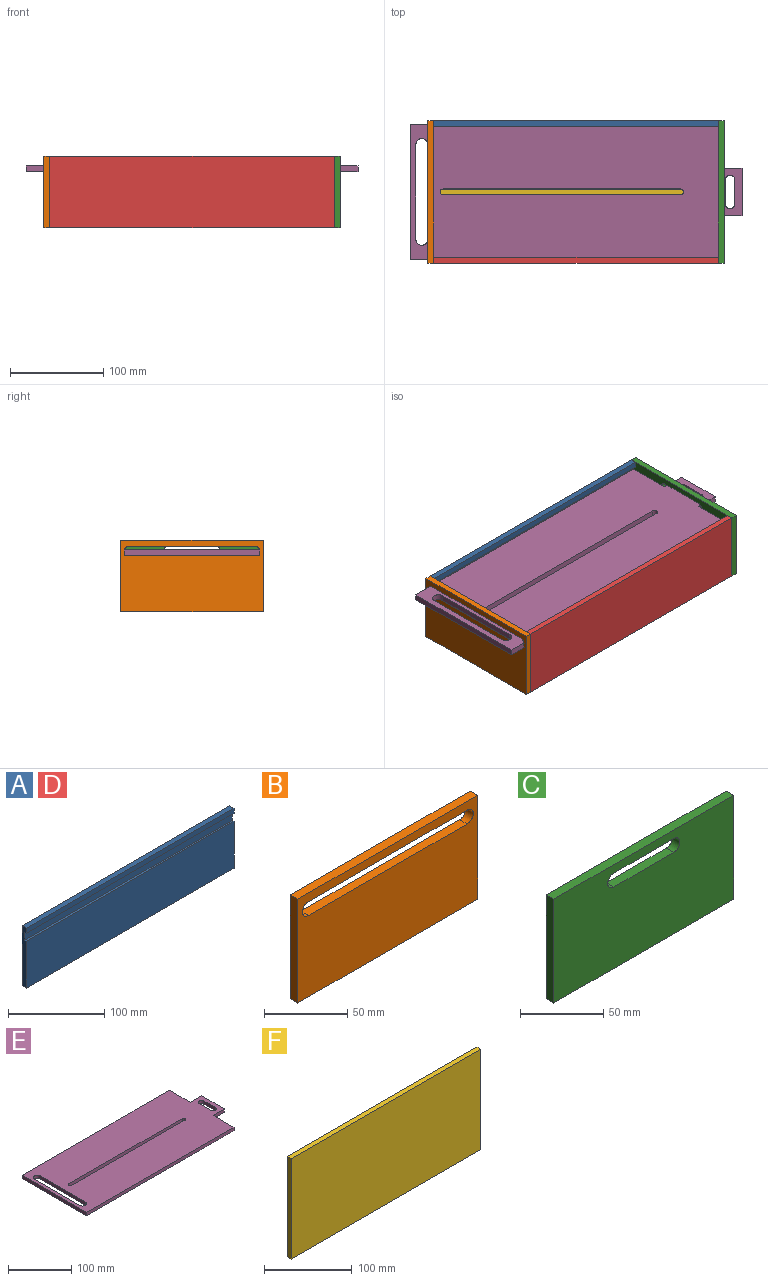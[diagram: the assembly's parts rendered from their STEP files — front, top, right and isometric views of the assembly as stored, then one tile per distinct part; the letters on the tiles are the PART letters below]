
ASSEMBLY  parts=6 mates=14
PART A: 10 faces, bbox 304.8x6.4x76.2 mm
  f0: plane 304.8x6.35mm, normal (0,-1,0), area 1935.5mm2, adj f1,f2,f4,f7
  f1: plane 76.2x6.35mm, normal (1,0,0), area 458.1mm2, adj f0,f3,f4,f5,f6,f7,f8,f9
  f2: plane 76.2x6.35mm, normal (-1,0,0), area 458.1mm2, adj f0,f3,f4,f5,f6,f7,f8,f9
  f3: plane 304.8x6.35mm, normal (0,0,-1), area 1935.5mm2, adj f1,f2,f5,f6
  f4: plane 304.8x6.35mm, normal (0,0,1), area 1935.5mm2, adj f0,f1,f2,f5
  f5: plane 304.8x76.2mm, normal (0,1,0), area 23225.8mm2, adj f1,f2,f3,f4
  f6: plane 304.8x59.69mm, normal (0,-1,0), area 18193.5mm2, adj f1,f2,f3,f8
  f7: plane 304.8x2.54mm, normal (0,0,-1), area 774.2mm2, adj f0,f1,f2,f9
  f8: plane 304.8x2.54mm, normal (0,0,1), area 774.2mm2, adj f1,f2,f6,f9
  f9: plane 304.8x10.16mm, normal (0,-1,0), area 3096.8mm2, adj f1,f2,f7,f8
PART B: 10 faces, bbox 152.4x6.4x76.2 mm
  f0: plane 152.4x6.35mm, normal (0,0,-1), area 967.7mm2, adj f1,f7,f8,f9
  f1: plane 76.2x6.35mm, normal (1,0,0), area 483.9mm2, adj f0,f2,f8,f9
  f2: plane 152.4x6.35mm, normal (0,0,1), area 967.7mm2, adj f1,f7,f8,f9
  f3: cylinder r=5.08mm len=10.16mm, axis (0,-1,0), area 101.3mm2, adj f4,f6,f8,f9
  f4: plane 134.62x6.35mm, normal (0,0,-1), area 854.8mm2, adj f3,f5,f8,f9
  f5: cylinder r=5.08mm len=10.16mm, axis (0,-1,0), area 101.3mm2, adj f4,f6,f8,f9
  f6: plane 134.62x6.35mm, normal (0,0,1), area 854.8mm2, adj f3,f5,f8,f9
  f7: plane 76.2x6.35mm, normal (-1,0,0), area 483.9mm2, adj f0,f2,f8,f9
  f8: plane 152.4x76.2mm, normal (0,1,0), area 10164.1mm2, adj f0,f1,f2,f3,f4,f5,f6,f7
  f9: plane 152.4x76.2mm, normal (0,-1,0), area 10164.1mm2, adj f0,f1,f2,f3,f4,f5,f6,f7
PART C: 10 faces, bbox 152.4x6.4x76.2 mm
  f0: plane 152.4x6.35mm, normal (0,0,-1), area 967.7mm2, adj f1,f7,f8,f9
  f1: plane 76.2x6.35mm, normal (1,0,0), area 483.9mm2, adj f0,f2,f8,f9
  f2: plane 152.4x6.35mm, normal (0,0,1), area 967.7mm2, adj f1,f7,f8,f9
  f3: cylinder r=5.08mm len=10.16mm, axis (0,-1,0), area 101.3mm2, adj f4,f6,f8,f9
  f4: plane 50.8x6.35mm, normal (0,0,-1), area 322.6mm2, adj f3,f5,f8,f9
  f5: cylinder r=5.08mm len=10.16mm, axis (0,-1,0), area 101.3mm2, adj f4,f6,f8,f9
  f6: plane 50.8x6.35mm, normal (0,0,1), area 322.6mm2, adj f3,f5,f8,f9
  f7: plane 76.2x6.35mm, normal (-1,0,0), area 483.9mm2, adj f0,f2,f8,f9
  f8: plane 152.4x76.2mm, normal (0,1,0), area 11015.7mm2, adj f0,f1,f2,f3,f4,f5,f6,f7
  f9: plane 152.4x76.2mm, normal (0,-1,0), area 11015.7mm2, adj f0,f1,f2,f3,f4,f5,f6,f7
PART D: same geometry as A
PART E: 22 faces, bbox 355.6x144.8x6.4 mm
  f0: plane 25.4x6.35mm, normal (0,1,0), area 161.3mm2, adj f1,f19,f20,f21
  f1: plane 46.99x6.35mm, normal (1,0,0), area 298.4mm2, adj f0,f2,f20,f21
  f2: plane 330.2x6.35mm, normal (0,1,0), area 2096.8mm2, adj f1,f3,f20,f21
  f3: plane 144.78x6.35mm, normal (-1,0,0), area 919.4mm2, adj f2,f4,f20,f21
  f4: plane 330.2x6.35mm, normal (0,-1,0), area 2096.8mm2, adj f3,f5,f20,f21
  f5: plane 46.99x6.35mm, normal (1,0,0), area 298.4mm2, adj f4,f6,f20,f21
  f6: plane 25.4x6.35mm, normal (0,-1,0), area 161.3mm2, adj f5,f19,f20,f21
  f7: cylinder r=5.08mm len=10.16mm, axis (0,0,1), area 101.3mm2, adj f8,f16,f20,f21
  f8: plane 25.4x6.35mm, normal (-1,0,0), area 161.3mm2, adj f7,f9,f20,f21
  f9: cylinder r=5.08mm len=10.16mm, axis (0,0,1), area 101.3mm2, adj f8,f16,f20,f21
  f10: cylinder r=3.17mm len=6.35mm, axis (0,0,1), area 63.3mm2, adj f11,f17,f20,f21
  f11: plane 254x6.35mm, normal (0,-1,0), area 1612.9mm2, adj f10,f12,f20,f21
  f12: cylinder r=3.17mm len=6.35mm, axis (0,0,1), area 63.3mm2, adj f11,f17,f20,f21
  f13: cylinder r=6.35mm len=12.7mm, axis (0,0,1), area 126.7mm2, adj f14,f18,f20,f21
  f14: plane 101.6x6.35mm, normal (-1,0,0), area 645.2mm2, adj f13,f15,f20,f21
  f15: cylinder r=6.35mm len=12.7mm, axis (0,0,1), area 126.7mm2, adj f14,f18,f20,f21
  f16: plane 25.4x6.35mm, normal (1,0,0), area 161.3mm2, adj f7,f9,f20,f21
  f17: plane 254x6.35mm, normal (0,1,0), area 1612.9mm2, adj f10,f12,f20,f21
  f18: plane 101.6x6.35mm, normal (1,0,0), area 645.2mm2, adj f13,f15,f20,f21
  f19: plane 50.8x6.35mm, normal (1,0,0), area 322.6mm2, adj f0,f6,f20,f21
  f20: plane 355.6x144.78mm, normal (0,0,-1), area 45696mm2, adj f0,f1,f2,f3,f4,f5,f6,f7
  f21: plane 355.6x144.78mm, normal (0,0,1), area 45696mm2, adj f0,f1,f2,f3,f4,f5,f6,f7
PART F: 6 faces, bbox 304.8x6.4x139.7 mm
  f0: plane 304.8x6.35mm, normal (0,0,-1), area 1935.5mm2, adj f1,f3,f4,f5
  f1: plane 139.7x6.35mm, normal (1,0,0), area 887.1mm2, adj f0,f2,f4,f5
  f2: plane 304.8x6.35mm, normal (0,0,1), area 1935.5mm2, adj f1,f3,f4,f5
  f3: plane 139.7x6.35mm, normal (-1,0,0), area 887.1mm2, adj f0,f2,f4,f5
  f4: plane 304.8x139.7mm, normal (0,1,0), area 42580.6mm2, adj f0,f1,f2,f3
  f5: plane 304.8x139.7mm, normal (0,-1,0), area 42580.6mm2, adj f0,f1,f2,f3
PLACE A rot(axis=(0.88,0.06,0.46),0deg) t=(105.65,-179.34,109.05)mm
PLACE B rot(axis=(0,0,-1),90deg) t=(-205.5,-325.39,109.05)mm
PLACE C rot(axis=(0,0,-1),90deg) t=(105.65,-325.39,109.05)mm
PLACE D rot(axis=(0,0,1),180deg) t=(-199.15,-319.04,109.05)mm
PLACE E rot(axis=(1,0,0),0deg) t=(105.65,-321.58,175.09)mm
PLACE F rot(axis=(-1,0,0),90deg) t=(105.65,-319.04,115.4)mm
MATE planar C.f0 <-> F.f4  axis (0,0,-1) through (108.83,-249.19,109.05)mm
MATE planar F.f1 <-> C.f9  axis (1,0,0) through (105.65,-249.19,112.23)mm
MATE planar F.f4 <-> B.f0  axis (0,0,-1) through (-46.75,-249.19,109.05)mm
MATE planar C.f1 <-> D.f5  axis (0,-1,0) through (108.83,-325.39,147.15)mm
MATE planar A.f1 <-> F.f1  axis (1,0,0) through (105.65,-176.05,145.65)mm
MATE planar F.f3 <-> B.f8  axis (-1,0,0) through (-199.15,-249.19,112.23)mm
MATE planar D.f3 <-> F.f4  axis (0,0,-1) through (-46.75,-322.21,109.05)mm
MATE planar F.f2 <-> A.f6  axis (0,1,0) through (-46.75,-179.34,112.23)mm
MATE planar D.f6 <-> F.f0  axis (0,1,0) through (-46.75,-319.04,138.9)mm
MATE planar F.f4 <-> A.f3  axis (0,0,-1) through (-46.75,-249.19,109.05)mm
MATE planar B.f6 <-> E.f20  axis (0,0,1) through (-199.15,-249.19,168.74)mm
MATE planar B.f1 <-> D.f5  axis (0,-1,0) through (-202.32,-325.39,147.15)mm
MATE planar E.f4 <-> D.f9  axis (0,-1,0) through (-224.55,-321.58,175.09)mm
MATE planar E.f5 <-> C.f9  axis (1,0,0) through (105.65,-298.08,171.92)mm
